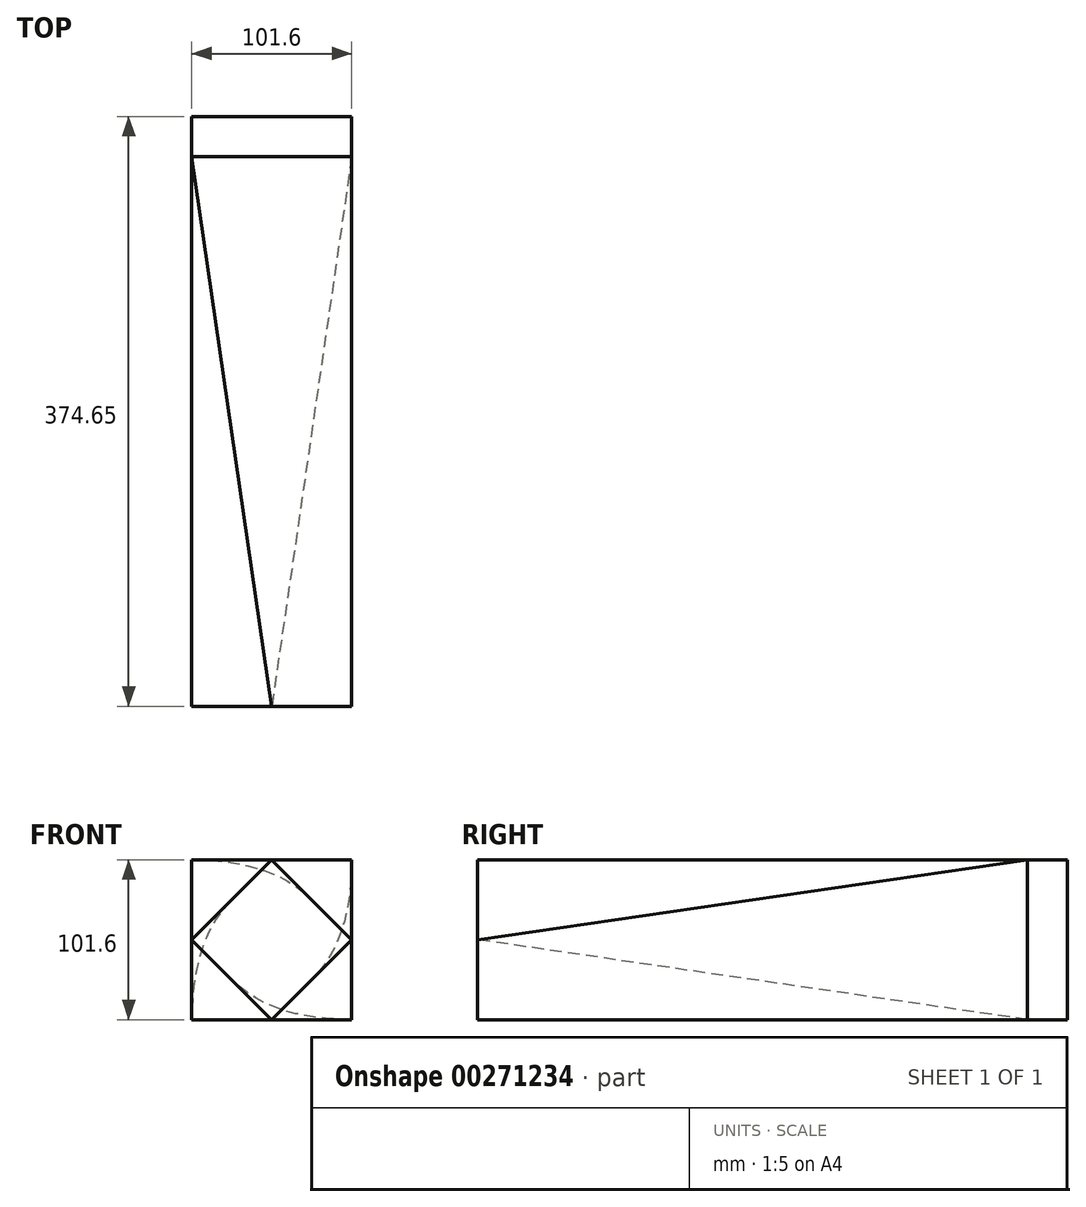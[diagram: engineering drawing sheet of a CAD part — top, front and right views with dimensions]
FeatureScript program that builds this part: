
annotation { "Feature Type Name" : "Feature", "Feature Type Description" : "" }
export const myFeature = defineFeature(function(context is Context, id is Id, definition is map)
    precondition{}
    {
        {
            var Q0;
            Q0=qCreatedBy(makeId("Front.planeOp"),FACE);
            var sketch = newSketch(context, id + "F0", { "sketchPlane" : qUnion([Q0])});
            skLineSegment(sketch, "E0.bottom", {"start": v(0, 0) * mm, "end": v(101.6, 0) * mm});
            skLineSegment(sketch, "E0.top", {"start": v(0, 101.6) * mm, "end": v(101.6, 101.6) * mm});
            skLineSegment(sketch, "E0.left", {"start": v(0, 0) * mm, "end": v(0, 101.6) * mm});
            skLineSegment(sketch, "E0.right", {"start": v(101.6, 0) * mm, "end": v(101.6, 101.6) * mm});
            skSolve(sketch);
        }
        {
            var Q0;
            Q0=makeQuery(id+"F0.imprint","IMPRINT",FACE,{"disambiguationData":[TD([[makeQuery(id+"F0.imprint","IMPRINT",EDGE,{"derivedFrom":sQuery(id+"F0.wireOp",EDGE,"E0.bottom")}),1.0]])]});
            extrude(context, id + "F1", {"entities" : qUnion([Q0]), "depth" : 25.4 * mm});
        }
        {
            var Q0;
            Q0=makeQuery(id+"F1.opExtrude","CAP_FACE",FACE,{"disambiguationData":[OSD([sQuery(id+"F0.wireOp",EDGE,"E0.bottom"),sQuery(id+"F0.wireOp",EDGE,"E0.top"),sQuery(id+"F0.wireOp",EDGE,"E0.left"),sQuery(id+"F0.wireOp",EDGE,"E0.right")])],"isStart":false});
            cPlane(context, id + "F2", {"entities" : qUnion([Q0]), "cplaneType" : CPlaneType.OFFSET, "offset" : 349.25 * mm, "width" : 152.4 * mm, "height" : 152.4 * mm});
        }
        {
            var Q0;
            Q0=qCreatedBy(id+"F2.planeOp",FACE);
            var sketch = newSketch(context, id + "F3", { "sketchPlane" : qUnion([Q0])});
            skLineSegment(sketch, "E1", {"start": v(50.8, 0) * mm, "end": v(0, 50.8) * mm});
            skLineSegment(sketch, "E2", {"start": v(0, 50.8) * mm, "end": v(50.8, 101.6) * mm});
            skLineSegment(sketch, "E3", {"start": v(50.8, 101.6) * mm, "end": v(101.6, 50.8) * mm});
            skLineSegment(sketch, "E4", {"start": v(101.6, 50.8) * mm, "end": v(50.8, 0) * mm});
            skSolve(sketch);
        }
        {
            var Q1;
            Q1=makeQuery(id+"F1.opExtrude","CAP_FACE",FACE,{"disambiguationData":[OSD([sQuery(id+"F0.wireOp",EDGE,"E0.bottom"),sQuery(id+"F0.wireOp",EDGE,"E0.top"),sQuery(id+"F0.wireOp",EDGE,"E0.left"),sQuery(id+"F0.wireOp",EDGE,"E0.right")])],"isStart":false});
            var Q2;
            Q2=makeQuery(id+"F3.imprint","IMPRINT",FACE,{"disambiguationData":[TD([[makeQuery(id+"F3.imprint","IMPRINT",EDGE,{"derivedFrom":sQuery(id+"F3.wireOp",EDGE,"E1")}),-1.0]])]});
            loft(context, id + "F4", {"operationType" : NewBodyOperationType.ADD, "sheetProfilesArray" : [{ "sheetProfileEntities" : qUnion([Q1]) }, { "sheetProfileEntities" : qUnion([Q2]) }]});
        }
    });
